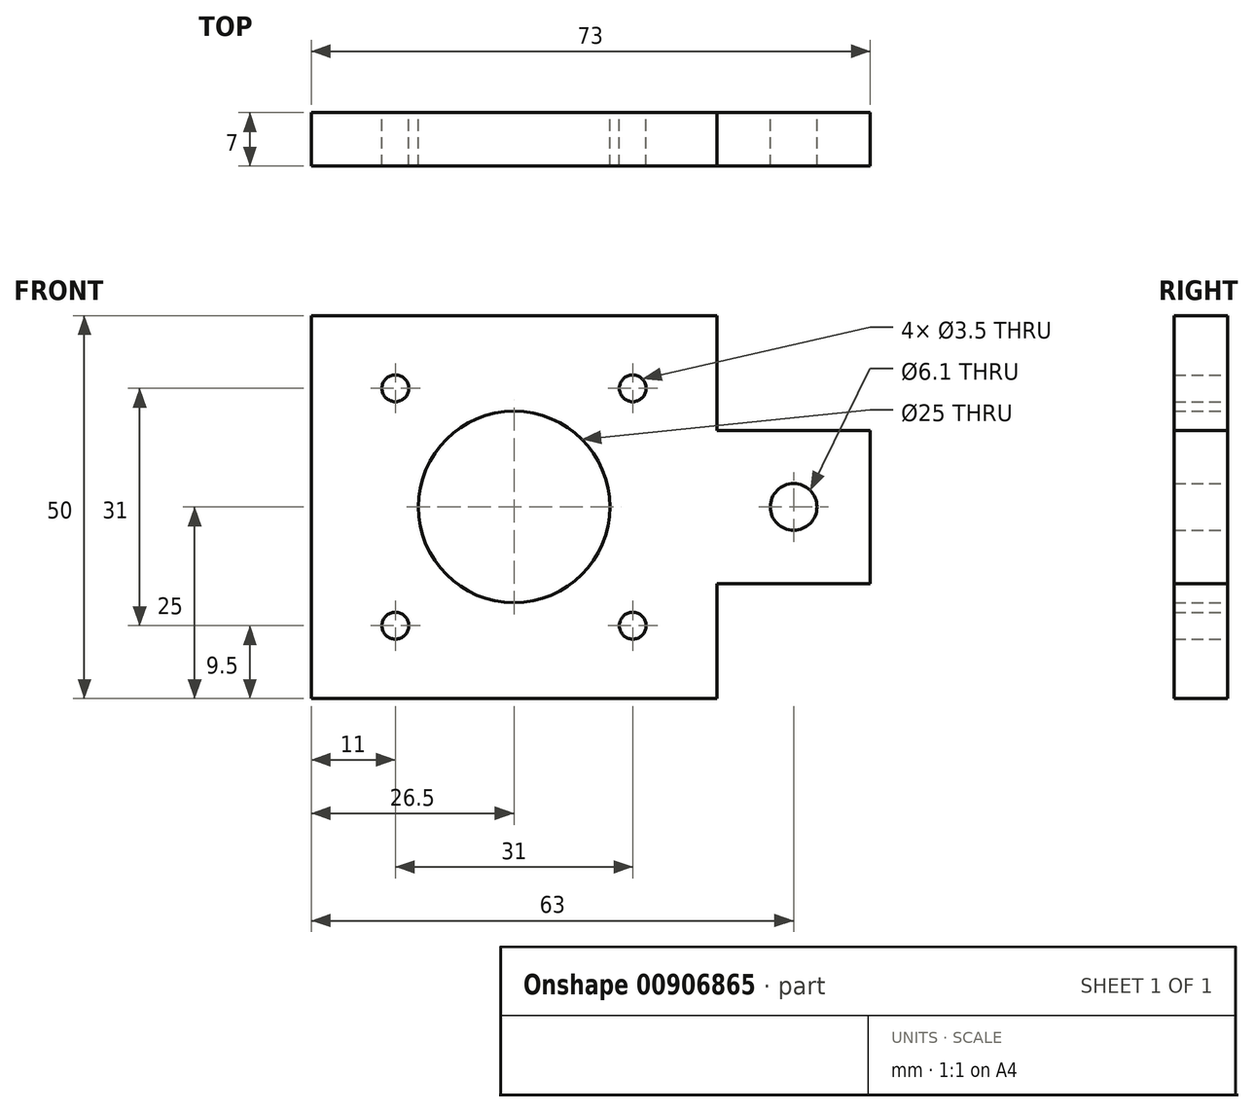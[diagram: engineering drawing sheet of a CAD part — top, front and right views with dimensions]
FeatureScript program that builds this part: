
annotation { "Feature Type Name" : "Feature", "Feature Type Description" : "" }
export const myFeature = defineFeature(function(context is Context, id is Id, definition is map)
    precondition{}
    {
        {
            var Q0;
            Q0=qCreatedBy(makeId("Front.planeOp"),FACE);
            var sketch = newSketch(context, id + "F0", { "sketchPlane" : qUnion([Q0])});
            skLineSegment(sketch, "E0.left", {"start": v(14.5, -10) * mm, "end": v(14.5, 10) * mm});
            skPoint(sketch, "E0.middle", {"position": v(2, 0) * mm});
            skCircle(sketch, "E1", {"center": v(4.5, 0) * mm, "radius": 3.05 * mm});
            skLineSegment(sketch, "E2", {"start": v(14.5, 10) * mm, "end": v(-17.5, 10) * mm});
            skLineSegment(sketch, "E3", {"start": v(-17.5, 10) * mm, "end": v(-17.5, -10) * mm});
            skLineSegment(sketch, "E4", {"start": v(-17.5, -10) * mm, "end": v(14.5, -10) * mm});
            skSolve(sketch);
        }
        {
            var Q0;
            Q0 = qSketchRegion(id + "F0", true);
            extrude(context, id + "F1", {"entities" : qUnion([Q0]), "depth" : 3 * mm, "offsetDistance" : 25 * mm});
        }
        {
            var Q0;
            Q0=makeQuery(id+"F1.opExtrude","CAP_FACE",FACE,{"disambiguationData":[OSD([sQuery(id+"F0.wireOp",EDGE,"E0.bottom"),sQuery(id+"F0.wireOp",EDGE,"E0.top"),sQuery(id+"F0.wireOp",EDGE,"E0.left"),sQuery(id+"F0.wireOp",EDGE,"E0.right"),sQuery(id+"F0.wireOp",EDGE,"E1")])],"isStart":true});
            var sketch = newSketch(context, id + "F2", { "sketchPlane" : qUnion([Q0])});
            skLineSegment(sketch, "E5.1", {"start": v(-14.5, -10) * mm, "end": v(-14.5, 10) * mm});
            skCircle(sketch, "E6", {"center": v(-4.5, 0) * mm, "radius": 3.05 * mm});
            skLineSegment(sketch, "E7.0", {"start": v(-14.5, 10) * mm, "end": v(17.5, 10) * mm});
            skLineSegment(sketch, "E7.1", {"start": v(17.5, 10) * mm, "end": v(17.5, -10) * mm});
            skLineSegment(sketch, "E7.2", {"start": v(17.5, -10) * mm, "end": v(-14.5, -10) * mm});
            skSolve(sketch);
        }
        {
            var Q0;
            Q0 = qSketchRegion(id + "F2", true);
            extrude(context, id + "F3", {"entities" : qUnion([Q0]), "operationType" : NewBodyOperationType.ADD, "depth" : 4 * mm, "offsetDistance" : 25 * mm});
        }
        {
            var Q0;
            Q0=makeQuery(id+"F3.opExtrude","CAP_FACE",FACE,{"disambiguationData":[OSD([sQuery(id+"F2.wireOp",EDGE,"E5.1"),sQuery(id+"F2.wireOp",EDGE,"E6"),sQuery(id+"F2.wireOp",EDGE,"E7.0"),sQuery(id+"F2.wireOp",EDGE,"E7.1"),sQuery(id+"F2.wireOp",EDGE,"E7.2")])],"isStart":false});
            var sketch = newSketch(context, id + "F4", { "sketchPlane" : qUnion([Q0])});
            skPoint(sketch, "E8.middle", {"position": v(11.5, 0) * mm});
            skLineSegment(sketch, "E9", {"start": v(5.5, 25) * mm, "end": v(5.5, -25) * mm});
            skLineSegment(sketch, "E10", {"start": v(5.5, 25) * mm, "end": v(58.5, 25) * mm});
            skLineSegment(sketch, "E11", {"start": v(58.5, 25) * mm, "end": v(58.5, -25) * mm});
            skLineSegment(sketch, "E12", {"start": v(58.5, -25) * mm, "end": v(5.5, -25) * mm});
            skCircle(sketch, "E13", {"center": v(32, 0) * mm, "radius": 12.5 * mm});
            skCircle(sketch, "E14", {"center": v(16.5, -15.5) * mm, "radius": 1.75 * mm});
            skCircle(sketch, "E15", {"center": v(47.5, -15.5) * mm, "radius": 1.75 * mm});
            skCircle(sketch, "E16", {"center": v(47.5, 15.5) * mm, "radius": 1.75 * mm});
            skCircle(sketch, "E17", {"center": v(16.5, 15.5) * mm, "radius": 1.75 * mm});
            skLineSegment(sketch, "E18", {"start": v(32, 25) * mm, "end": v(32, -25) * mm, "construction": true});
            skSolve(sketch);
        }
        {
            var Q0;
            {var subQ5=makeQuery(id+"F3.opExtrude","CAP_EDGE",EDGE,{"disambiguationData":[OSD([sQuery(id+"F2.wireOp",EDGE,"E7.1")])],"isStart":false});Q0=makeQuery(id+"F4.imprint","IMPRINT",FACE,{"disambiguationData":[TD([[makeQuery(id+"F4.imprint","IMPRINT",EDGE,{"derivedFrom":subQ5}),-1.0]])]});}
            var sketch = newSketch(context, id + "F5", { "sketchPlane" : qUnion([Q0])});
            skLineSegment(sketch, "E19.0.0", {"start": v(17.5, 10) * mm, "end": v(5.5, 10) * mm});
            skLineSegment(sketch, "E19.0.1", {"start": v(5.5, 10) * mm, "end": v(5.5, -10) * mm});
            skLineSegment(sketch, "E19.0.2", {"start": v(5.5, -10) * mm, "end": v(17.5, -10) * mm});
            skLineSegment(sketch, "E19.0.3", {"start": v(17.5, -10) * mm, "end": v(17.5, 10) * mm});
            skSolve(sketch);
        }
        {
            var Q0;
            Q0 = qSketchRegion(id + "F5", true);
            extrude(context, id + "F6", {"entities" : qUnion([Q0]), "operationType" : NewBodyOperationType.REMOVE, "endBound" : BoundingType.THROUGH_ALL, "oppositeDirection" : true, "depth" : 25 * mm, "offsetDistance" : 25 * mm});
        }
        {
            var Q0;
            Q0 = qSketchRegion(id + "F4", true);
            extrude(context, id + "F7", {"entities" : qUnion([Q0]), "operationType" : NewBodyOperationType.ADD, "oppositeDirection" : true, "depth" : 7 * mm, "offsetDistance" : 25 * mm});
        }
        {
            var Q0;
            Q0=qCreatedBy(makeId("Right.planeOp"),FACE);
            cPlane(context, id + "F8", {"entities" : qUnion([Q0]), "cplaneType" : CPlaneType.OFFSET, "offset" : 32 * mm, "oppositeDirection" : true, "width" : 150 * mm, "height" : 150 * mm});
        }
        {
            var Q0;
            Q0=makeQuery(id+"F1.opExtrude","SWEPT_BODY",BODY,{"disambiguationData":[OSD([sQuery(id+"F0.wireOp",EDGE,"E0.left"),sQuery(id+"F0.wireOp",EDGE,"E1"),sQuery(id+"F0.wireOp",EDGE,"E2"),sQuery(id+"F0.wireOp",EDGE,"E3"),sQuery(id+"F0.wireOp",EDGE,"E4")])]});
            var Q1;
            Q1=qCreatedBy(id+"F8.planeOp",FACE);
            mirror(context, id + "F9", {"operationType" : NewBodyOperationType.ADD, "entities" : qUnion([Q0]), "mirrorPlane" : qUnion([Q1])});
        }
        {
            var Q0;
            Q0=qCreatedBy(makeId("Front.planeOp"),FACE);
            var sketch = newSketch(context, id + "F10", { "sketchPlane" : qUnion([Q0])});
            skLineSegment(sketch, "E20.bottom", {"start": v(-58.5, 10) * mm, "end": v(-97.17, 10) * mm});
            skLineSegment(sketch, "E20.top", {"start": v(-58.5, -16) * mm, "end": v(-97.17, -16) * mm});
            skLineSegment(sketch, "E20.left", {"start": v(-58.5, 10) * mm, "end": v(-58.5, -16) * mm});
            skLineSegment(sketch, "E20.right", {"start": v(-97.17, 10) * mm, "end": v(-97.17, -16) * mm});
            skSolve(sketch);
        }
        {
            var Q0;
            Q0 = qSketchRegion(id + "F10", true);
            extrude(context, id + "F11", {"entities" : qUnion([Q0]), "operationType" : NewBodyOperationType.REMOVE, "endBound" : BoundingType.SYMMETRIC, "oppositeDirection" : true, "depth" : 25 * mm, "offsetDistance" : 25 * mm});
        }
    });
